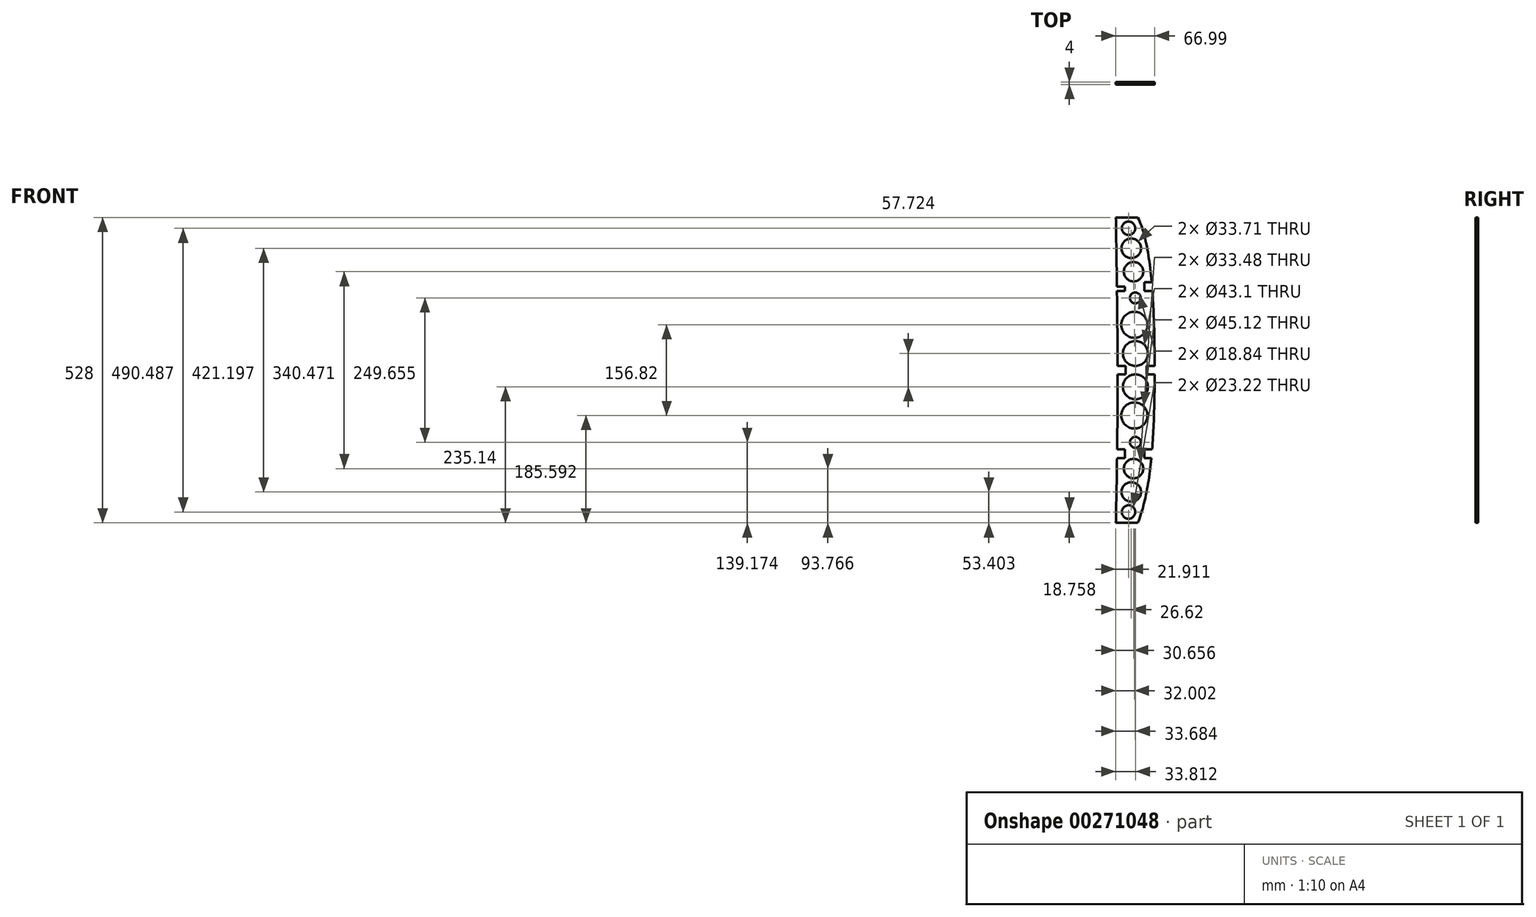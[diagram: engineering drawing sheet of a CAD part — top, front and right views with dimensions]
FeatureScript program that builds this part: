
annotation { "Feature Type Name" : "Feature", "Feature Type Description" : "" }
export const myFeature = defineFeature(function(context is Context, id is Id, definition is map)
    precondition{}
    {
        {
            var Q0;
            Q0=qCreatedBy(makeId("Front.planeOp"),FACE);
            var sketch = newSketch(context, id + "F0", { "sketchPlane" : qUnion([Q0])});
            skLineSegment(sketch, "E0", {"start": v(128.85, -6.84) * mm, "end": v(61.85, -6.84) * mm});
            skLineSegment(sketch, "E1", {"start": v(61.85, -6.84) * mm, "end": v(61.85, 257.16) * mm});
            skLineSegment(sketch, "E2", {"start": v(61.85, 257.16) * mm, "end": v(99.85, 257.16) * mm});
            skLineSegment(sketch, "E3.MirrorCS", {"start": v(61.85, -6.84) * mm, "end": v(61.85, -270.84) * mm});
            skLineSegment(sketch, "E4.MirrorCS", {"start": v(61.85, -270.84) * mm, "end": v(99.85, -270.84) * mm});
            skFitSpline(sketch, "E5", {"points": [v(99.85, 257.16) * mm, v(128.85, -6.84) * mm, v(99.85, -270.84) * mm], "startDerivative": vector(148.45, -292.3) * mm, "endDerivative": vector(-148.45, -368.58) * mm});
            skLineSegment(sketch, "E6", {"start": v(61.85, -6.84) * mm, "end": v(64.85, -6.84) * mm});
            skFitSpline(sketch, "E7", {"points": [v(61.85, 257.16) * mm, v(64.85, -6.84) * mm, v(61.85, -270.84) * mm], "startDerivative": vector(9, -528) * mm, "endDerivative": vector(-12.19, -529.62) * mm});
            skLineSegment(sketch, "E8", {"start": v(114.84, -6.84) * mm, "end": v(114.84, 0.66) * mm});
            skLineSegment(sketch, "E9", {"start": v(114.84, 0.66) * mm, "end": v(128.84, 0.66) * mm});
            skLineSegment(sketch, "E10", {"start": v(78.83, -6.84) * mm, "end": v(78.83, 0.66) * mm});
            skLineSegment(sketch, "E11", {"start": v(78.83, 0.66) * mm, "end": v(64.83, 0.66) * mm});
            skLineSegment(sketch, "E12.MirrorCS", {"start": v(114.84, -6.84) * mm, "end": v(114.84, -14.34) * mm});
            skLineSegment(sketch, "E13.MirrorCS", {"start": v(114.84, -14.34) * mm, "end": v(128.84, -14.34) * mm});
            skLineSegment(sketch, "E14.MirrorCS", {"start": v(78.83, -6.84) * mm, "end": v(78.83, -14.34) * mm});
            skLineSegment(sketch, "E15.MirrorCS", {"start": v(78.83, -14.34) * mm, "end": v(64.83, -14.34) * mm});
            skLineSegment(sketch, "E16", {"start": v(148.2, 137.66) * mm, "end": v(36.32, 137.66) * mm});
            skLineSegment(sketch, "E17", {"start": v(110.9, 137.66) * mm, "end": v(110.9, 130.16) * mm});
            skLineSegment(sketch, "E18", {"start": v(110.9, 130.16) * mm, "end": v(124.9, 130.16) * mm});
            skLineSegment(sketch, "E19", {"start": v(77.8, 137.66) * mm, "end": v(77.8, 130.16) * mm});
            skLineSegment(sketch, "E20", {"start": v(77.8, 130.16) * mm, "end": v(63.8, 130.16) * mm});
            skLineSegment(sketch, "E21.MirrorCS", {"start": v(110.9, 137.66) * mm, "end": v(110.9, 145.16) * mm});
            skLineSegment(sketch, "E22.MirrorCS", {"start": v(110.9, 145.16) * mm, "end": v(124.9, 145.16) * mm});
            skLineSegment(sketch, "E23.MirrorCS", {"start": v(77.8, 137.66) * mm, "end": v(77.8, 145.16) * mm});
            skLineSegment(sketch, "E24.MirrorCS", {"start": v(77.8, 145.16) * mm, "end": v(63.8, 145.16) * mm});
            skCircle(sketch, "E25", {"center": v(95.66, 22.02) * mm, "radius": 21.55 * mm});
            skCircle(sketch, "E26", {"center": v(93.85, 71.57) * mm, "radius": 22.56 * mm});
            skCircle(sketch, "E27", {"center": v(92.5, 163.4) * mm, "radius": 16.74 * mm});
            skCircle(sketch, "E28", {"center": v(88.47, 203.76) * mm, "radius": 16.85 * mm});
            skCircle(sketch, "E29", {"center": v(83.76, 238.4) * mm, "radius": 11.6 * mm});
            skCircle(sketch, "E30", {"center": v(95.53, 117.99) * mm, "radius": 9.42 * mm});
            skCircle(sketch, "E31.MirrorC", {"center": v(95.53, -131.67) * mm, "radius": 9.42 * mm});
            skCircle(sketch, "E32.MirrorC", {"center": v(93.85, -85.25) * mm, "radius": 22.56 * mm});
            skCircle(sketch, "E33.MirrorC", {"center": v(95.66, -35.7) * mm, "radius": 21.55 * mm});
            skLineSegment(sketch, "E34.MirrorCS", {"start": v(77.8, -151.34) * mm, "end": v(77.8, -143.84) * mm});
            skLineSegment(sketch, "E35.MirrorCS", {"start": v(77.8, -151.34) * mm, "end": v(77.8, -158.84) * mm});
            skLineSegment(sketch, "E36.MirrorCS", {"start": v(110.9, -151.34) * mm, "end": v(110.9, -158.84) * mm});
            skLineSegment(sketch, "E37.MirrorCS", {"start": v(110.9, -151.34) * mm, "end": v(110.9, -143.84) * mm});
            skLineSegment(sketch, "E38.MirrorCS", {"start": v(110.9, -158.84) * mm, "end": v(124.9, -158.84) * mm});
            skLineSegment(sketch, "E39.MirrorCS", {"start": v(77.8, -143.84) * mm, "end": v(63.8, -143.84) * mm});
            skLineSegment(sketch, "E40.MirrorCS", {"start": v(77.8, -158.84) * mm, "end": v(63.8, -158.84) * mm});
            skLineSegment(sketch, "E41.MirrorCS", {"start": v(110.9, -143.84) * mm, "end": v(124.9, -143.84) * mm});
            skCircle(sketch, "E42.MirrorC", {"center": v(92.5, -177.07) * mm, "radius": 16.74 * mm});
            skCircle(sketch, "E43.MirrorC", {"center": v(88.47, -217.44) * mm, "radius": 16.85 * mm});
            skCircle(sketch, "E44.MirrorC", {"center": v(83.76, -252.08) * mm, "radius": 11.6 * mm});
            skSolve(sketch);
        }
        {
            var Q0;
            {var subQ7=sQuery(id+"F0.wireOp",EDGE,"E8");Q0=makeQuery(id+"F0.imprint","IMPRINT",FACE,{"disambiguationData":[TD([[makeQuery(id+"F0.imprint","IMPRINT",EDGE,{"derivedFrom":subQ7}),1.0]])]});}
            var Q1;
            {var subQ1=sQuery(id+"F0.wireOp",EDGE,"E2");Q1=makeQuery(id+"F0.imprint","IMPRINT",FACE,{"disambiguationData":[TD([[makeQuery(id+"F0.imprint","IMPRINT",EDGE,{"derivedFrom":subQ1}),-1.0]])]});}
            var Q2;
            {var subQ15=sQuery(id+"F0.wireOp",EDGE,"E4.MirrorCS");Q2=makeQuery(id+"F0.imprint","IMPRINT",FACE,{"disambiguationData":[TD([[makeQuery(id+"F0.imprint","IMPRINT",EDGE,{"derivedFrom":subQ15}),1.0]])]});}
            extrude(context, id + "F1", {"entities" : qUnion([Q0, Q1, Q2]), "depth" : 4 * mm});
        }
    });
